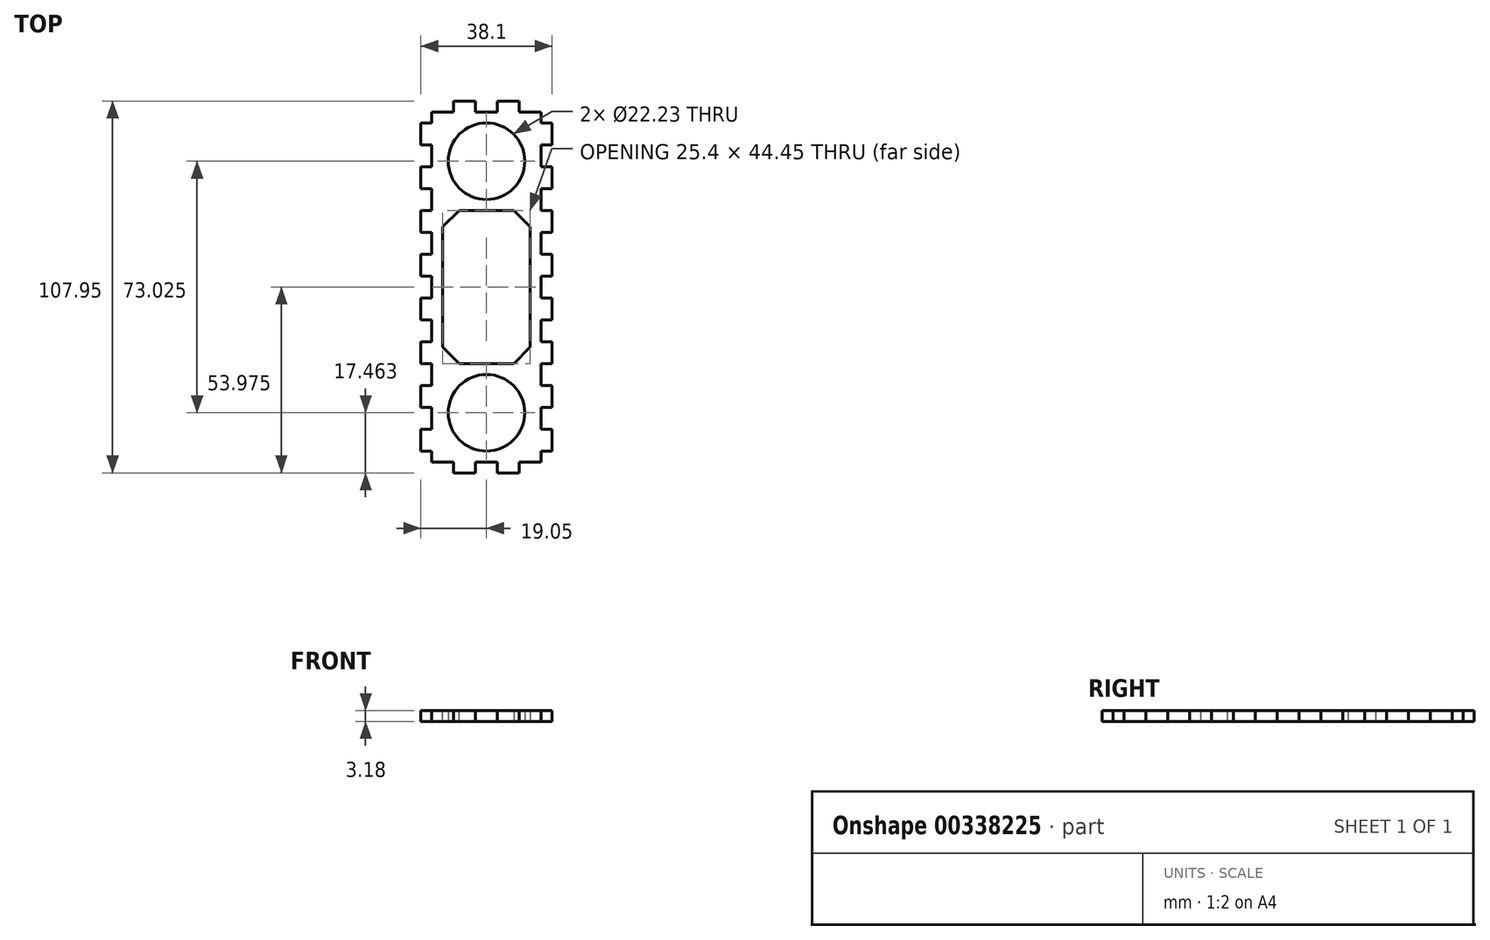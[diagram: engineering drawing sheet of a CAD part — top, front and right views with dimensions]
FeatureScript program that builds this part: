
annotation { "Feature Type Name" : "Feature", "Feature Type Description" : "" }
export const myFeature = defineFeature(function(context is Context, id is Id, definition is map)
    precondition{}
    {
        {
            var Q0;
            Q0=qCreatedBy(makeId("Top.planeOp"),FACE);
            var sketch = newSketch(context, id + "F0", { "sketchPlane" : qUnion([Q0])});
            skLineSegment(sketch, "E0.bottom", {"start": v(0, 0) * mm, "end": v(38.1, 0) * mm});
            skLineSegment(sketch, "E0.top", {"start": v(0, -107.95) * mm, "end": v(38.1, -107.95) * mm});
            skLineSegment(sketch, "E0.left", {"start": v(0, 0) * mm, "end": v(0, -107.95) * mm});
            skLineSegment(sketch, "E0.right", {"start": v(38.1, 0) * mm, "end": v(38.1, -107.95) * mm});
            skLineSegment(sketch, "E1", {"start": v(19.05, 0) * mm, "end": v(19.05, -17.46) * mm, "construction": true});
            skCircle(sketch, "E2", {"center": v(19.05, -17.46) * mm, "radius": 11.11 * mm});
            skLineSegment(sketch, "E3", {"start": v(19.05, -17.46) * mm, "end": v(19.05, -90.49) * mm, "construction": true});
            skLineSegment(sketch, "E4", {"start": v(19.05, -90.49) * mm, "end": v(19.05, -107.95) * mm, "construction": true});
            skCircle(sketch, "E5", {"center": v(19.05, -90.49) * mm, "radius": 11.11 * mm});
            skSolve(sketch);
        }
        {
            var Q0;
            Q0 = qSketchRegion(id + "F0", true);
            extrude(context, id + "F1", {"entities" : qUnion([Q0]), "depth" : 3.17 * mm});
        }
        {
            var Q0;
            Q0=makeQuery(id+"F1.opExtrude","CAP_FACE",FACE,{"disambiguationData":[OSD([sQuery(id+"F0.wireOp",EDGE,"E0.bottom"),sQuery(id+"F0.wireOp",EDGE,"E0.top"),sQuery(id+"F0.wireOp",EDGE,"E0.left"),sQuery(id+"F0.wireOp",EDGE,"E0.right"),sQuery(id+"F0.wireOp",EDGE,"E2"),sQuery(id+"F0.wireOp",EDGE,"E5")])],"isStart":false});
            var sketch = newSketch(context, id + "F2", { "sketchPlane" : qUnion([Q0])});
            skLineSegment(sketch, "E6.bottom", {"start": v(38.1, 0) * mm, "end": v(34.93, 0) * mm});
            skLineSegment(sketch, "E6.top", {"start": v(38.1, -6.35) * mm, "end": v(34.93, -6.35) * mm});
            skLineSegment(sketch, "E6.left", {"start": v(38.1, 0) * mm, "end": v(38.1, -6.35) * mm});
            skLineSegment(sketch, "E6.right", {"start": v(34.93, 0) * mm, "end": v(34.93, -6.35) * mm});
            skLineSegment(sketch, "E7.bottom", {"start": v(0, 0) * mm, "end": v(3.17, 0) * mm});
            skLineSegment(sketch, "E7.top", {"start": v(0, -6.35) * mm, "end": v(3.17, -6.35) * mm});
            skLineSegment(sketch, "E7.left", {"start": v(0, 0) * mm, "end": v(0, -6.35) * mm});
            skLineSegment(sketch, "E7.right", {"start": v(3.17, 0) * mm, "end": v(3.17, -6.35) * mm});
            skLineSegment(sketch, "E8", {"start": v(3.17, -6.35) * mm, "end": v(3.17, -12.7) * mm, "construction": true});
            skLineSegment(sketch, "E9.bottom", {"start": v(3.17, -12.7) * mm, "end": v(0, -12.7) * mm});
            skLineSegment(sketch, "E9.top", {"start": v(3.17, -19.05) * mm, "end": v(0, -19.05) * mm});
            skLineSegment(sketch, "E9.left", {"start": v(3.17, -12.7) * mm, "end": v(3.17, -19.05) * mm});
            skLineSegment(sketch, "E9.right", {"start": v(0, -12.7) * mm, "end": v(0, -19.05) * mm});
            skLineSegment(sketch, "E10", {"start": v(34.93, -6.35) * mm, "end": v(34.93, -12.7) * mm, "construction": true});
            skLineSegment(sketch, "E11.bottom", {"start": v(34.93, -12.7) * mm, "end": v(38.1, -12.7) * mm});
            skLineSegment(sketch, "E11.top", {"start": v(34.93, -19.05) * mm, "end": v(38.1, -19.05) * mm});
            skLineSegment(sketch, "E11.left", {"start": v(34.93, -12.7) * mm, "end": v(34.93, -19.05) * mm});
            skLineSegment(sketch, "E11.right", {"start": v(38.1, -12.7) * mm, "end": v(38.1, -19.05) * mm});
            skLineSegment(sketch, "E12.0.1.0", {"start": v(34.93, -25.4) * mm, "end": v(38.1, -25.4) * mm});
            skLineSegment(sketch, "E12.0.1.1", {"start": v(34.93, -31.75) * mm, "end": v(38.1, -31.75) * mm});
            skLineSegment(sketch, "E12.0.1.2", {"start": v(34.93, -19.05) * mm, "end": v(34.93, -25.4) * mm, "construction": true});
            skLineSegment(sketch, "E12.0.1.3", {"start": v(38.1, -25.4) * mm, "end": v(38.1, -31.75) * mm});
            skLineSegment(sketch, "E12.0.1.4", {"start": v(34.93, -25.4) * mm, "end": v(34.93, -31.75) * mm});
            skLineSegment(sketch, "E12.0.2.0", {"start": v(34.93, -38.1) * mm, "end": v(38.1, -38.1) * mm});
            skLineSegment(sketch, "E12.0.2.1", {"start": v(34.93, -44.45) * mm, "end": v(38.1, -44.45) * mm});
            skLineSegment(sketch, "E12.0.2.2", {"start": v(34.93, -31.75) * mm, "end": v(34.93, -38.1) * mm, "construction": true});
            skLineSegment(sketch, "E12.0.2.3", {"start": v(38.1, -38.1) * mm, "end": v(38.1, -44.45) * mm});
            skLineSegment(sketch, "E12.0.2.4", {"start": v(34.93, -38.1) * mm, "end": v(34.93, -44.45) * mm});
            skLineSegment(sketch, "E12.0.3.0", {"start": v(34.93, -50.8) * mm, "end": v(38.1, -50.8) * mm});
            skLineSegment(sketch, "E12.0.3.1", {"start": v(34.93, -57.15) * mm, "end": v(38.1, -57.15) * mm});
            skLineSegment(sketch, "E12.0.3.2", {"start": v(34.93, -44.45) * mm, "end": v(34.93, -50.8) * mm, "construction": true});
            skLineSegment(sketch, "E12.0.3.3", {"start": v(38.1, -50.8) * mm, "end": v(38.1, -57.15) * mm});
            skLineSegment(sketch, "E12.0.3.4", {"start": v(34.93, -50.8) * mm, "end": v(34.93, -57.15) * mm});
            skLineSegment(sketch, "E12.0.4.0", {"start": v(34.93, -63.5) * mm, "end": v(38.1, -63.5) * mm});
            skLineSegment(sketch, "E12.0.4.1", {"start": v(34.93, -69.85) * mm, "end": v(38.1, -69.85) * mm});
            skLineSegment(sketch, "E12.0.4.2", {"start": v(34.93, -57.15) * mm, "end": v(34.93, -63.5) * mm, "construction": true});
            skLineSegment(sketch, "E12.0.4.3", {"start": v(38.1, -63.5) * mm, "end": v(38.1, -69.85) * mm});
            skLineSegment(sketch, "E12.0.4.4", {"start": v(34.93, -63.5) * mm, "end": v(34.93, -69.85) * mm});
            skLineSegment(sketch, "E12.0.5.0", {"start": v(34.93, -76.2) * mm, "end": v(38.1, -76.2) * mm});
            skLineSegment(sketch, "E12.0.5.1", {"start": v(34.93, -82.55) * mm, "end": v(38.1, -82.55) * mm});
            skLineSegment(sketch, "E12.0.5.2", {"start": v(34.93, -69.85) * mm, "end": v(34.93, -76.2) * mm, "construction": true});
            skLineSegment(sketch, "E12.0.5.3", {"start": v(38.1, -76.2) * mm, "end": v(38.1, -82.55) * mm});
            skLineSegment(sketch, "E12.0.5.4", {"start": v(34.93, -76.2) * mm, "end": v(34.93, -82.55) * mm});
            skLineSegment(sketch, "E12.0.6.0", {"start": v(34.93, -88.9) * mm, "end": v(38.1, -88.9) * mm});
            skLineSegment(sketch, "E12.0.6.1", {"start": v(34.93, -95.25) * mm, "end": v(38.1, -95.25) * mm});
            skLineSegment(sketch, "E12.0.6.2", {"start": v(34.93, -82.55) * mm, "end": v(34.93, -88.9) * mm, "construction": true});
            skLineSegment(sketch, "E12.0.6.3", {"start": v(38.1, -88.9) * mm, "end": v(38.1, -95.25) * mm});
            skLineSegment(sketch, "E12.0.6.4", {"start": v(34.93, -88.9) * mm, "end": v(34.93, -95.25) * mm});
            skLineSegment(sketch, "E12.0.7.0", {"start": v(34.93, -101.6) * mm, "end": v(38.1, -101.6) * mm});
            skLineSegment(sketch, "E12.0.7.1", {"start": v(34.93, -107.95) * mm, "end": v(38.1, -107.95) * mm});
            skLineSegment(sketch, "E12.0.7.2", {"start": v(34.93, -95.25) * mm, "end": v(34.93, -101.6) * mm, "construction": true});
            skLineSegment(sketch, "E12.0.7.3", {"start": v(38.1, -101.6) * mm, "end": v(38.1, -107.95) * mm});
            skLineSegment(sketch, "E12.0.7.4", {"start": v(34.93, -101.6) * mm, "end": v(34.93, -107.95) * mm});
            skLineSegment(sketch, "E12.0.8.0", {"start": v(34.93, -114.3) * mm, "end": v(38.1, -114.3) * mm});
            skLineSegment(sketch, "E12.0.8.1", {"start": v(34.93, -120.65) * mm, "end": v(38.1, -120.65) * mm});
            skLineSegment(sketch, "E12.0.8.2", {"start": v(34.93, -107.95) * mm, "end": v(34.93, -114.3) * mm, "construction": true});
            skLineSegment(sketch, "E12.0.8.3", {"start": v(38.1, -114.3) * mm, "end": v(38.1, -120.65) * mm});
            skLineSegment(sketch, "E12.0.8.4", {"start": v(34.93, -114.3) * mm, "end": v(34.93, -120.65) * mm});
            skLineSegment(sketch, "E12.0.9.0", {"start": v(34.93, -127) * mm, "end": v(38.1, -127) * mm});
            skLineSegment(sketch, "E12.0.9.1", {"start": v(34.93, -133.35) * mm, "end": v(38.1, -133.35) * mm});
            skLineSegment(sketch, "E12.0.9.2", {"start": v(34.93, -120.65) * mm, "end": v(34.93, -127) * mm, "construction": true});
            skLineSegment(sketch, "E12.0.9.3", {"start": v(38.1, -127) * mm, "end": v(38.1, -133.35) * mm});
            skLineSegment(sketch, "E12.0.9.4", {"start": v(34.93, -127) * mm, "end": v(34.93, -133.35) * mm});
            skLineSegment(sketch, "E12.direction1", {"start": v(17.46, -19.05) * mm, "end": v(34.93, -19.05) * mm, "construction": true});
            skLineSegment(sketch, "E12.direction2", {"start": v(34.93, -19.05) * mm, "end": v(34.93, -31.75) * mm, "construction": true});
            skLineSegment(sketch, "E13.0.1.0", {"start": v(3.17, -19.05) * mm, "end": v(3.17, -25.4) * mm, "construction": true});
            skLineSegment(sketch, "E13.0.1.1", {"start": v(3.17, -25.4) * mm, "end": v(0, -25.4) * mm});
            skLineSegment(sketch, "E13.0.1.2", {"start": v(3.17, -31.75) * mm, "end": v(0, -31.75) * mm});
            skLineSegment(sketch, "E13.0.1.3", {"start": v(3.17, -25.4) * mm, "end": v(3.17, -31.75) * mm});
            skLineSegment(sketch, "E13.0.1.4", {"start": v(0, -25.4) * mm, "end": v(0, -31.75) * mm});
            skLineSegment(sketch, "E13.0.2.0", {"start": v(3.17, -31.75) * mm, "end": v(3.17, -38.1) * mm, "construction": true});
            skLineSegment(sketch, "E13.0.2.1", {"start": v(3.17, -38.1) * mm, "end": v(0, -38.1) * mm});
            skLineSegment(sketch, "E13.0.2.2", {"start": v(3.17, -44.45) * mm, "end": v(0, -44.45) * mm});
            skLineSegment(sketch, "E13.0.2.3", {"start": v(3.17, -38.1) * mm, "end": v(3.17, -44.45) * mm});
            skLineSegment(sketch, "E13.0.2.4", {"start": v(0, -38.1) * mm, "end": v(0, -44.45) * mm});
            skLineSegment(sketch, "E13.0.3.0", {"start": v(3.17, -44.45) * mm, "end": v(3.17, -50.8) * mm, "construction": true});
            skLineSegment(sketch, "E13.0.3.1", {"start": v(3.17, -50.8) * mm, "end": v(0, -50.8) * mm});
            skLineSegment(sketch, "E13.0.3.2", {"start": v(3.17, -57.15) * mm, "end": v(0, -57.15) * mm});
            skLineSegment(sketch, "E13.0.3.3", {"start": v(3.17, -50.8) * mm, "end": v(3.17, -57.15) * mm});
            skLineSegment(sketch, "E13.0.3.4", {"start": v(0, -50.8) * mm, "end": v(0, -57.15) * mm});
            skLineSegment(sketch, "E13.0.4.0", {"start": v(3.17, -57.15) * mm, "end": v(3.17, -63.5) * mm, "construction": true});
            skLineSegment(sketch, "E13.0.4.1", {"start": v(3.17, -63.5) * mm, "end": v(0, -63.5) * mm});
            skLineSegment(sketch, "E13.0.4.2", {"start": v(3.17, -69.85) * mm, "end": v(0, -69.85) * mm});
            skLineSegment(sketch, "E13.0.4.3", {"start": v(3.17, -63.5) * mm, "end": v(3.17, -69.85) * mm});
            skLineSegment(sketch, "E13.0.4.4", {"start": v(0, -63.5) * mm, "end": v(0, -69.85) * mm});
            skLineSegment(sketch, "E13.0.5.0", {"start": v(3.17, -69.85) * mm, "end": v(3.17, -76.2) * mm, "construction": true});
            skLineSegment(sketch, "E13.0.5.1", {"start": v(3.17, -76.2) * mm, "end": v(0, -76.2) * mm});
            skLineSegment(sketch, "E13.0.5.2", {"start": v(3.17, -82.55) * mm, "end": v(0, -82.55) * mm});
            skLineSegment(sketch, "E13.0.5.3", {"start": v(3.17, -76.2) * mm, "end": v(3.17, -82.55) * mm});
            skLineSegment(sketch, "E13.0.5.4", {"start": v(0, -76.2) * mm, "end": v(0, -82.55) * mm});
            skLineSegment(sketch, "E13.0.6.0", {"start": v(3.17, -82.55) * mm, "end": v(3.17, -88.9) * mm, "construction": true});
            skLineSegment(sketch, "E13.0.6.1", {"start": v(3.17, -88.9) * mm, "end": v(0, -88.9) * mm});
            skLineSegment(sketch, "E13.0.6.2", {"start": v(3.17, -95.25) * mm, "end": v(0, -95.25) * mm});
            skLineSegment(sketch, "E13.0.6.3", {"start": v(3.17, -88.9) * mm, "end": v(3.17, -95.25) * mm});
            skLineSegment(sketch, "E13.0.6.4", {"start": v(0, -88.9) * mm, "end": v(0, -95.25) * mm});
            skLineSegment(sketch, "E13.0.7.0", {"start": v(3.17, -95.25) * mm, "end": v(3.17, -101.6) * mm, "construction": true});
            skLineSegment(sketch, "E13.0.7.1", {"start": v(3.17, -101.6) * mm, "end": v(0, -101.6) * mm});
            skLineSegment(sketch, "E13.0.7.2", {"start": v(3.17, -107.95) * mm, "end": v(0, -107.95) * mm});
            skLineSegment(sketch, "E13.0.7.3", {"start": v(3.17, -101.6) * mm, "end": v(3.17, -107.95) * mm});
            skLineSegment(sketch, "E13.0.7.4", {"start": v(0, -101.6) * mm, "end": v(0, -107.95) * mm});
            skLineSegment(sketch, "E13.0.8.0", {"start": v(3.17, -107.95) * mm, "end": v(3.17, -114.3) * mm, "construction": true});
            skLineSegment(sketch, "E13.0.8.1", {"start": v(3.17, -114.3) * mm, "end": v(0, -114.3) * mm});
            skLineSegment(sketch, "E13.0.8.2", {"start": v(3.17, -120.65) * mm, "end": v(0, -120.65) * mm});
            skLineSegment(sketch, "E13.0.8.3", {"start": v(3.17, -114.3) * mm, "end": v(3.17, -120.65) * mm});
            skLineSegment(sketch, "E13.0.8.4", {"start": v(0, -114.3) * mm, "end": v(0, -120.65) * mm});
            skLineSegment(sketch, "E13.0.9.0", {"start": v(3.17, -120.65) * mm, "end": v(3.17, -127) * mm, "construction": true});
            skLineSegment(sketch, "E13.0.9.1", {"start": v(3.17, -127) * mm, "end": v(0, -127) * mm});
            skLineSegment(sketch, "E13.0.9.2", {"start": v(3.17, -133.35) * mm, "end": v(0, -133.35) * mm});
            skLineSegment(sketch, "E13.0.9.3", {"start": v(3.17, -127) * mm, "end": v(3.17, -133.35) * mm});
            skLineSegment(sketch, "E13.0.9.4", {"start": v(0, -127) * mm, "end": v(0, -133.35) * mm});
            skLineSegment(sketch, "E13.direction1", {"start": v(0, -19.05) * mm, "end": v(17.46, -19.05) * mm, "construction": true});
            skLineSegment(sketch, "E13.direction2", {"start": v(0, -19.05) * mm, "end": v(0, -31.75) * mm, "construction": true});
            skLineSegment(sketch, "E14", {"start": v(19.05, 0) * mm, "end": v(19.05, -17.46) * mm, "construction": true});
            skLineSegment(sketch, "E15", {"start": v(19.05, -17.46) * mm, "end": v(19.05, -31.75) * mm, "construction": true});
            skLineSegment(sketch, "E16.bottom", {"start": v(6.35, -31.75) * mm, "end": v(31.75, -31.75) * mm});
            skLineSegment(sketch, "E16.top", {"start": v(6.35, -76.2) * mm, "end": v(31.75, -76.2) * mm});
            skLineSegment(sketch, "E16.left", {"start": v(6.35, -31.75) * mm, "end": v(6.35, -76.2) * mm});
            skLineSegment(sketch, "E16.right", {"start": v(31.75, -31.75) * mm, "end": v(31.75, -76.2) * mm});
            skLineSegment(sketch, "E17", {"start": v(31.75, -53.97) * mm, "end": v(34.93, -53.97) * mm, "construction": true});
            skLineSegment(sketch, "E18", {"start": v(19.05, -76.2) * mm, "end": v(19.05, -90.49) * mm, "construction": true});
            skLineSegment(sketch, "E19", {"start": v(19.05, -90.49) * mm, "end": v(19.05, -107.95) * mm, "construction": true});
            skSolve(sketch);
        }
        {
            var Q0;
            Q0 = qSketchRegion(id + "F2", true);
            var Q1;
            Q1=makeQuery(id+"F1.opExtrude","CAP_FACE",FACE,{"disambiguationData":[OSD([sQuery(id+"F0.wireOp",EDGE,"E0.bottom"),sQuery(id+"F0.wireOp",EDGE,"E0.top"),sQuery(id+"F0.wireOp",EDGE,"E0.left"),sQuery(id+"F0.wireOp",EDGE,"E0.right"),sQuery(id+"F0.wireOp",EDGE,"E2"),sQuery(id+"F0.wireOp",EDGE,"E5")])],"isStart":true});
            extrude(context, id + "F3", {"entities" : qUnion([Q0]), "operationType" : NewBodyOperationType.REMOVE, "endBound" : BoundingType.UP_TO_SURFACE, "oppositeDirection" : true, "endBoundEntityFace" : qUnion([Q1]), "depth" : 25.4 * mm});
        }
        {
            var Q0;
            Q0=makeQuery(id+"F1.opExtrude","CAP_FACE",FACE,{"disambiguationData":[OSD([sQuery(id+"F0.wireOp",EDGE,"E0.bottom"),sQuery(id+"F0.wireOp",EDGE,"E0.top"),sQuery(id+"F0.wireOp",EDGE,"E0.left"),sQuery(id+"F0.wireOp",EDGE,"E0.right"),sQuery(id+"F0.wireOp",EDGE,"E2"),sQuery(id+"F0.wireOp",EDGE,"E5")])],"isStart":false});
            var sketch = newSketch(context, id + "F4", { "sketchPlane" : qUnion([Q0])});
            skLineSegment(sketch, "E20.bottom", {"start": v(15.88, 0) * mm, "end": v(22.23, 0) * mm});
            skLineSegment(sketch, "E20.top", {"start": v(15.88, -3.18) * mm, "end": v(22.23, -3.18) * mm});
            skLineSegment(sketch, "E20.left", {"start": v(15.88, 0) * mm, "end": v(15.88, -3.18) * mm});
            skLineSegment(sketch, "E20.right", {"start": v(22.23, 0) * mm, "end": v(22.23, -3.18) * mm});
            skLineSegment(sketch, "E21.bottom", {"start": v(28.58, 0) * mm, "end": v(34.93, 0) * mm});
            skLineSegment(sketch, "E21.top", {"start": v(28.58, -3.18) * mm, "end": v(34.93, -3.18) * mm});
            skLineSegment(sketch, "E21.left", {"start": v(28.58, 0) * mm, "end": v(28.58, -3.18) * mm});
            skLineSegment(sketch, "E21.right", {"start": v(34.93, 0) * mm, "end": v(34.93, -3.18) * mm});
            skLineSegment(sketch, "E22", {"start": v(15.88, -3.18) * mm, "end": v(9.53, -3.18) * mm, "construction": true});
            skLineSegment(sketch, "E23", {"start": v(28.58, -3.18) * mm, "end": v(22.23, -3.18) * mm, "construction": true});
            skLineSegment(sketch, "E24.bottom", {"start": v(9.53, -3.18) * mm, "end": v(3.17, -3.18) * mm});
            skLineSegment(sketch, "E24.top", {"start": v(9.53, 0) * mm, "end": v(3.17, 0) * mm});
            skLineSegment(sketch, "E24.left", {"start": v(9.53, -3.18) * mm, "end": v(9.53, 0) * mm});
            skLineSegment(sketch, "E24.right", {"start": v(3.17, -3.18) * mm, "end": v(3.17, 0) * mm});
            skLineSegment(sketch, "E25.bottom", {"start": v(34.93, -107.95) * mm, "end": v(28.58, -107.95) * mm});
            skLineSegment(sketch, "E25.top", {"start": v(34.93, -104.78) * mm, "end": v(28.58, -104.78) * mm});
            skLineSegment(sketch, "E25.left", {"start": v(34.93, -107.95) * mm, "end": v(34.93, -104.78) * mm});
            skLineSegment(sketch, "E25.right", {"start": v(28.58, -107.95) * mm, "end": v(28.58, -104.78) * mm});
            skLineSegment(sketch, "E26.bottom", {"start": v(3.18, -107.95) * mm, "end": v(9.53, -107.95) * mm});
            skLineSegment(sketch, "E26.top", {"start": v(3.18, -104.78) * mm, "end": v(9.53, -104.78) * mm});
            skLineSegment(sketch, "E26.left", {"start": v(3.18, -107.95) * mm, "end": v(3.18, -104.78) * mm});
            skLineSegment(sketch, "E26.right", {"start": v(9.53, -107.95) * mm, "end": v(9.53, -104.78) * mm});
            skLineSegment(sketch, "E27.bottom", {"start": v(15.88, -107.95) * mm, "end": v(22.23, -107.95) * mm});
            skLineSegment(sketch, "E27.top", {"start": v(15.88, -104.78) * mm, "end": v(22.23, -104.78) * mm});
            skLineSegment(sketch, "E27.left", {"start": v(15.88, -107.95) * mm, "end": v(15.88, -104.78) * mm});
            skLineSegment(sketch, "E27.right", {"start": v(22.23, -107.95) * mm, "end": v(22.23, -104.78) * mm});
            skLineSegment(sketch, "E28", {"start": v(9.53, -104.78) * mm, "end": v(15.88, -104.78) * mm, "construction": true});
            skLineSegment(sketch, "E29", {"start": v(22.23, -104.78) * mm, "end": v(28.58, -104.78) * mm, "construction": true});
            skSolve(sketch);
        }
        {
            var Q0;
            Q0 = qSketchRegion(id + "F4", true);
            var Q1;
            Q1=makeQuery(id+"F1.opExtrude","CAP_FACE",FACE,{"disambiguationData":[OSD([sQuery(id+"F0.wireOp",EDGE,"E0.bottom"),sQuery(id+"F0.wireOp",EDGE,"E0.top"),sQuery(id+"F0.wireOp",EDGE,"E0.left"),sQuery(id+"F0.wireOp",EDGE,"E0.right"),sQuery(id+"F0.wireOp",EDGE,"E2"),sQuery(id+"F0.wireOp",EDGE,"E5")])],"isStart":true});
            extrude(context, id + "F5", {"entities" : qUnion([Q0]), "operationType" : NewBodyOperationType.REMOVE, "endBound" : BoundingType.UP_TO_SURFACE, "oppositeDirection" : true, "endBoundEntityFace" : qUnion([Q1]), "depth" : 25.4 * mm});
        }
        {
            var Q0;
            Q0=makeQuery(id+"F3.boolean.opBoolean","COPY",EDGE,{"derivedFrom":makeQuery(id+"F3.opExtrude","SWEPT_EDGE",EDGE,{"disambiguationData":[OSD([sQuery(id+"F2.wireOp",EDGE,"E16.bottom"),sQuery(id+"F2.wireOp",EDGE,"E16.right")])]})});
            var Q1;
            Q1=makeQuery(id+"F3.boolean.opBoolean","COPY",EDGE,{"derivedFrom":makeQuery(id+"F3.opExtrude","SWEPT_EDGE",EDGE,{"disambiguationData":[OSD([sQuery(id+"F2.wireOp",EDGE,"E16.bottom"),sQuery(id+"F2.wireOp",EDGE,"E16.left")])]})});
            var Q2;
            Q2=makeQuery(id+"F3.boolean.opBoolean","COPY",EDGE,{"derivedFrom":makeQuery(id+"F3.opExtrude","SWEPT_EDGE",EDGE,{"disambiguationData":[OSD([sQuery(id+"F2.wireOp",EDGE,"E16.top"),sQuery(id+"F2.wireOp",EDGE,"E16.left")])]})});
            var Q3;
            Q3=makeQuery(id+"F3.boolean.opBoolean","COPY",EDGE,{"derivedFrom":makeQuery(id+"F3.opExtrude","SWEPT_EDGE",EDGE,{"disambiguationData":[OSD([sQuery(id+"F2.wireOp",EDGE,"E16.top"),sQuery(id+"F2.wireOp",EDGE,"E16.right")])]})});
            chamfer(context, id + "F6", {"entities" : qUnion([Q0, Q1, Q2, Q3]), "width" : 4.76 * mm, "tangentPropagation" : true});
        }
    });
